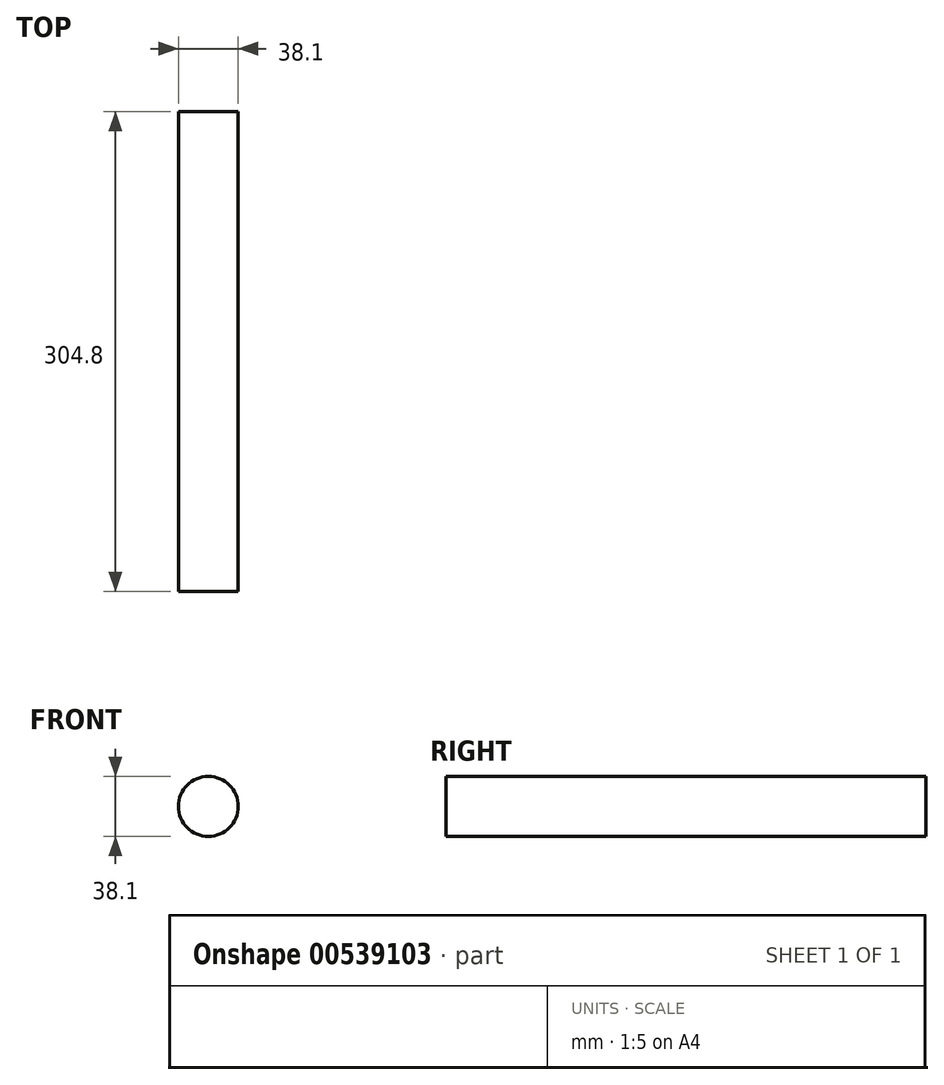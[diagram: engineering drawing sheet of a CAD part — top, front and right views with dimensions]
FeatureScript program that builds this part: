
annotation { "Feature Type Name" : "Feature", "Feature Type Description" : "" }
export const myFeature = defineFeature(function(context is Context, id is Id, definition is map)
    precondition{}
    {
        {
            var Q0;
            Q0=qCreatedBy(makeId("Front.planeOp"),FACE);
            var sketch = newSketch(context, id + "F0", { "sketchPlane" : qUnion([Q0])});
            skCircle(sketch, "E0", {"center": v(0, 0) * mm, "radius": 19.05 * mm});
            skSolve(sketch);
        }
        {
            var Q0;
            Q0 = qSketchRegion(id + "F0", true);
            extrude(context, id + "F1", {"entities" : qUnion([Q0]), "oppositeDirection" : true, "depth" : 304.8 * mm, "offsetDistance" : 25.4 * mm});
        }
    });
